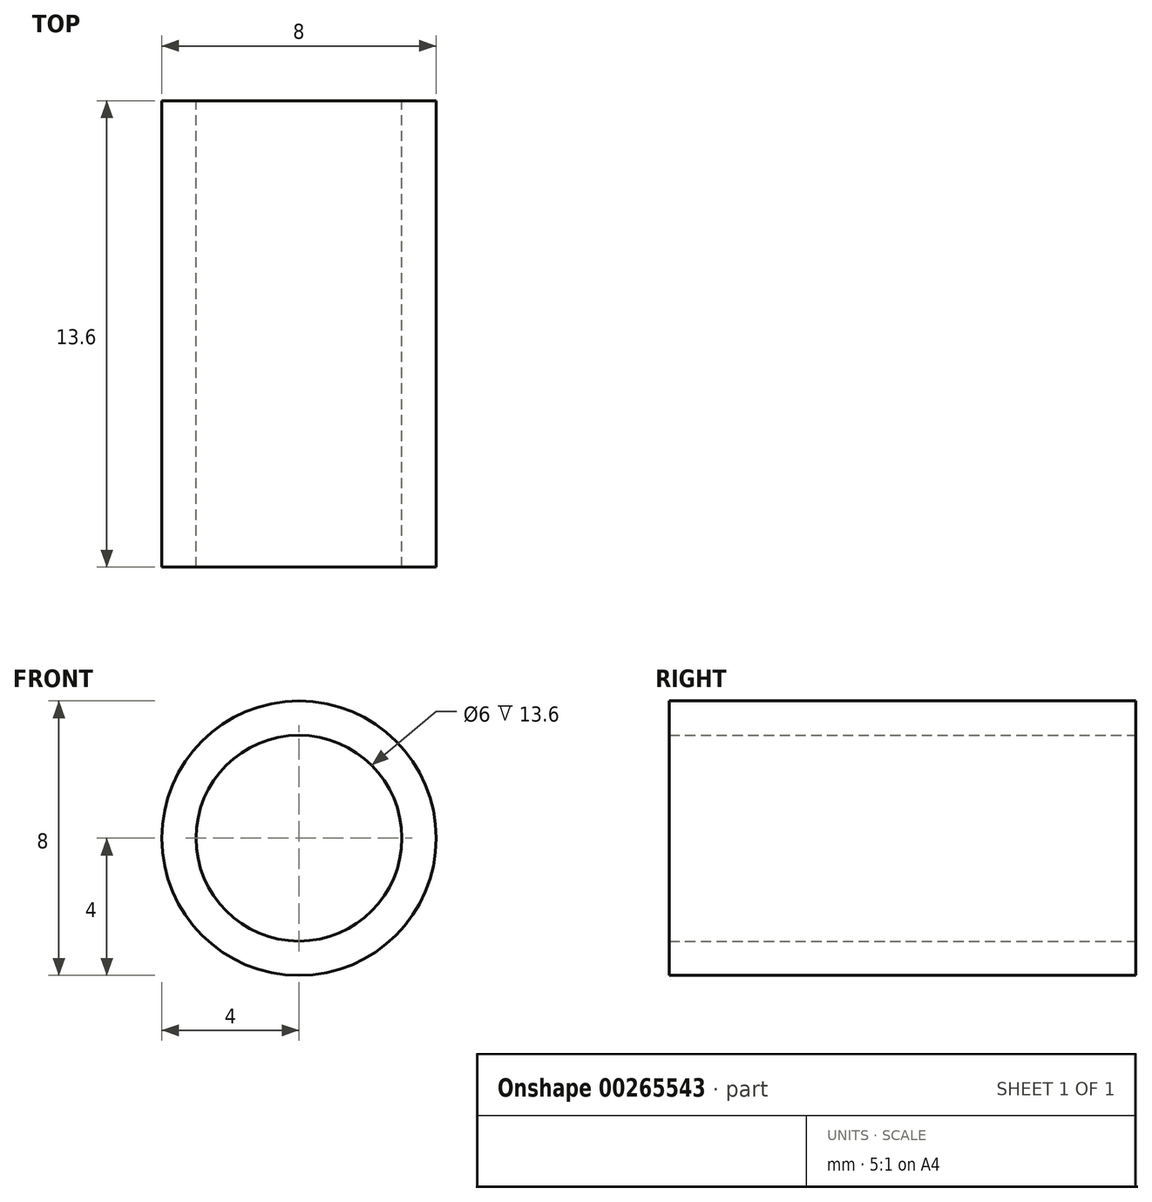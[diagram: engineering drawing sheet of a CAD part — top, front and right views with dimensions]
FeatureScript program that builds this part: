
annotation { "Feature Type Name" : "Feature", "Feature Type Description" : "" }
export const myFeature = defineFeature(function(context is Context, id is Id, definition is map)
    precondition{}
    {
        {
            var Q0;
            Q0=qCreatedBy(makeId("Front.planeOp"),FACE);
            var sketch = newSketch(context, id + "F0", { "sketchPlane" : qUnion([Q0])});
            skCircle(sketch, "E0", {"center": v(0, 0) * mm, "radius": 4 * mm});
            skCircle(sketch, "E1", {"center": v(0, 0) * mm, "radius": 3 * mm});
            skSolve(sketch);
        }
        {
            var Q0;
            Q0=makeQuery(id+"F0.imprint","IMPRINT",FACE,{"disambiguationData":[TD([[makeQuery(id+"F0.imprint","IMPRINT",EDGE,{"derivedFrom":sQuery(id+"F0.wireOp",EDGE,"E0")}),1.0]])]});
            extrude(context, id + "F1", {"entities" : qUnion([Q0]), "depth" : 13.6 * mm});
        }
    });
